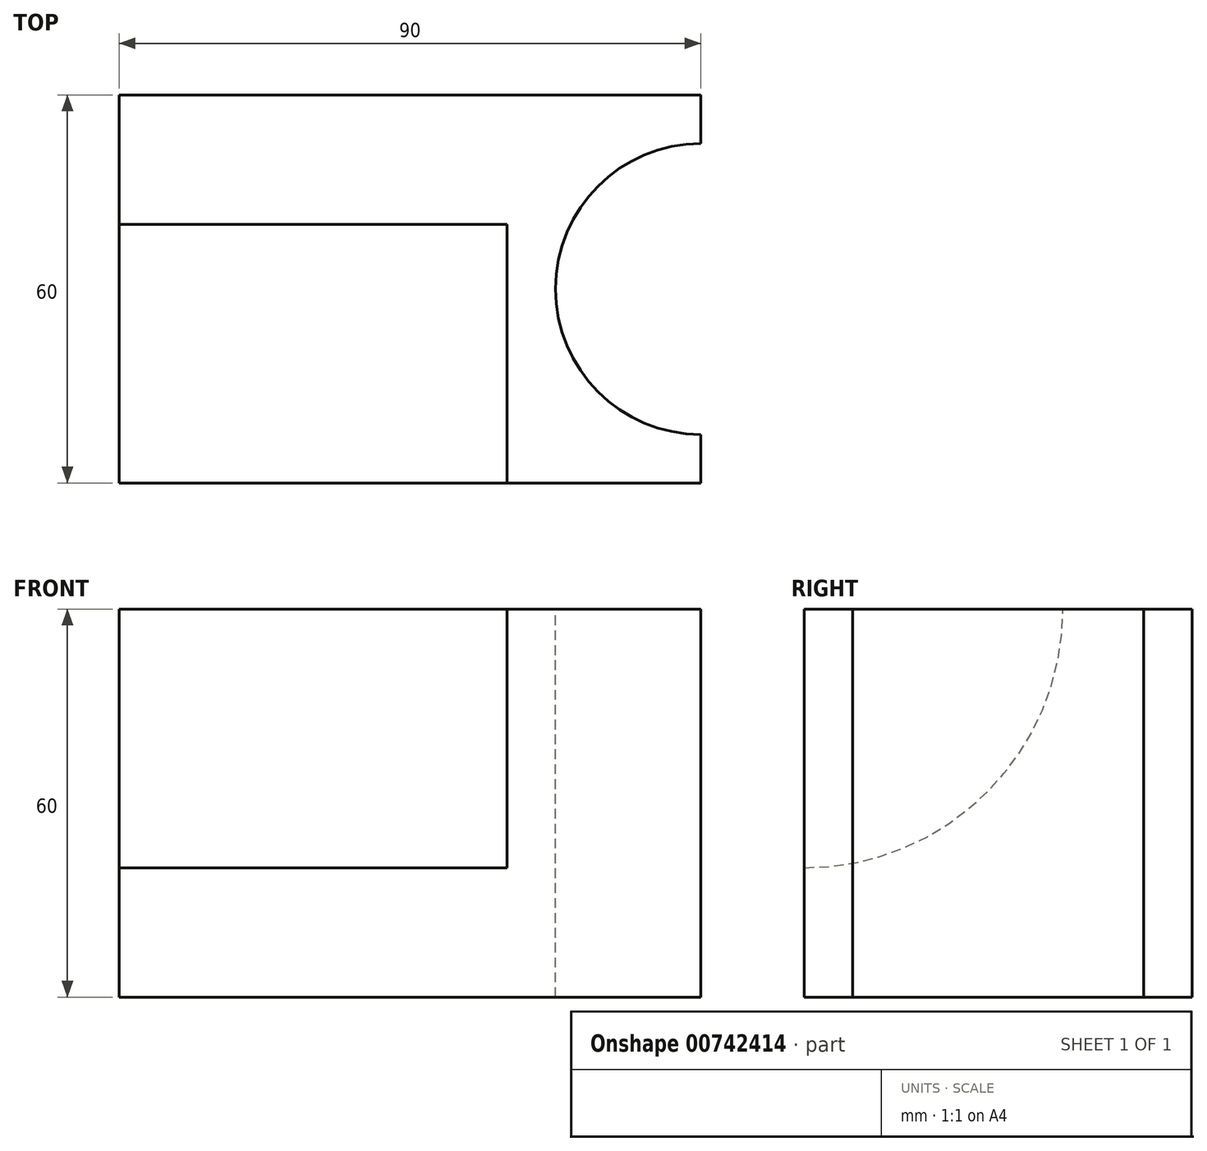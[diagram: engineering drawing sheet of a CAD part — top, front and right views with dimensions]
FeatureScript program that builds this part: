
annotation { "Feature Type Name" : "Feature", "Feature Type Description" : "" }
export const myFeature = defineFeature(function(context is Context, id is Id, definition is map)
    precondition{}
    {
        {
            var Q0;
            Q0=qCreatedBy(makeId("Front.planeOp"),FACE);
            var sketch = newSketch(context, id + "F0", { "sketchPlane" : qUnion([Q0])});
            skLineSegment(sketch, "E0.bottom", {"start": v(0, 0) * mm, "end": v(90, 0) * mm});
            skLineSegment(sketch, "E0.top", {"start": v(0, 60) * mm, "end": v(90, 60) * mm});
            skLineSegment(sketch, "E0.left", {"start": v(0, 0) * mm, "end": v(0, 60) * mm});
            skLineSegment(sketch, "E0.right", {"start": v(90, 0) * mm, "end": v(90, 60) * mm});
            skSolve(sketch);
        }
        {
            var Q0;
            Q0=makeQuery(id+"F0.imprint","IMPRINT",FACE,{"disambiguationData":[TD([[makeQuery(id+"F0.imprint","IMPRINT",EDGE,{"derivedFrom":sQuery(id+"F0.wireOp",EDGE,"E0.bottom")}),1.0]])]});
            extrude(context, id + "F1", {"entities" : qUnion([Q0]), "depth" : 60 * mm, "offsetDistance" : 25 * mm});
        }
        {
            var Q0;
            Q0=makeQuery(id+"F1.opExtrude","SWEPT_FACE",FACE,{"disambiguationData":[OSD([sQuery(id+"F0.wireOp",EDGE,"E0.top")])]});
            var sketch = newSketch(context, id + "F2", { "sketchPlane" : qUnion([Q0])});
            skArc(sketch, "E1", {"start": v(90, -7.5) * mm, "mid": v(67.5, -30) * mm, "end": v(90, -52.5) * mm});
            skSolve(sketch);
        }
        {
            var Q0;
            {var subQ0=sQuery(id+"F2.wireOp",EDGE,"E1");Q0=makeQuery(id+"F2.imprint","IMPRINT",FACE,{"disambiguationData":[TD([[makeQuery(id+"F2.imprint","IMPRINT",EDGE,{"derivedFrom":subQ0}),1.0]])]});}
            extrude(context, id + "F3", {"entities" : qUnion([Q0]), "operationType" : NewBodyOperationType.REMOVE, "endBound" : BoundingType.SYMMETRIC, "oppositeDirection" : true, "depth" : 127.2 * mm, "offsetDistance" : 25 * mm});
        }
        {
            var Q0;
            Q0=makeQuery(id+"F1.opExtrude","SWEPT_FACE",FACE,{"disambiguationData":[OSD([sQuery(id+"F0.wireOp",EDGE,"E0.left")])]});
            var sketch = newSketch(context, id + "F4", { "sketchPlane" : qUnion([Q0])});
            skArc(sketch, "E2", {"start": v(20, 60) * mm, "mid": v(31.72, 31.72) * mm, "end": v(60, 20) * mm});
            skSolve(sketch);
        }
        {
            var Q0;
            {var subQ0=sQuery(id+"F4.wireOp",EDGE,"E2");Q0=makeQuery(id+"F4.imprint","IMPRINT",FACE,{"disambiguationData":[TD([[makeQuery(id+"F4.imprint","IMPRINT",EDGE,{"derivedFrom":subQ0}),1.0]])]});}
            extrude(context, id + "F5", {"entities" : qUnion([Q0]), "operationType" : NewBodyOperationType.REMOVE, "oppositeDirection" : true, "depth" : 60 * mm, "offsetDistance" : 25 * mm});
        }
    });
